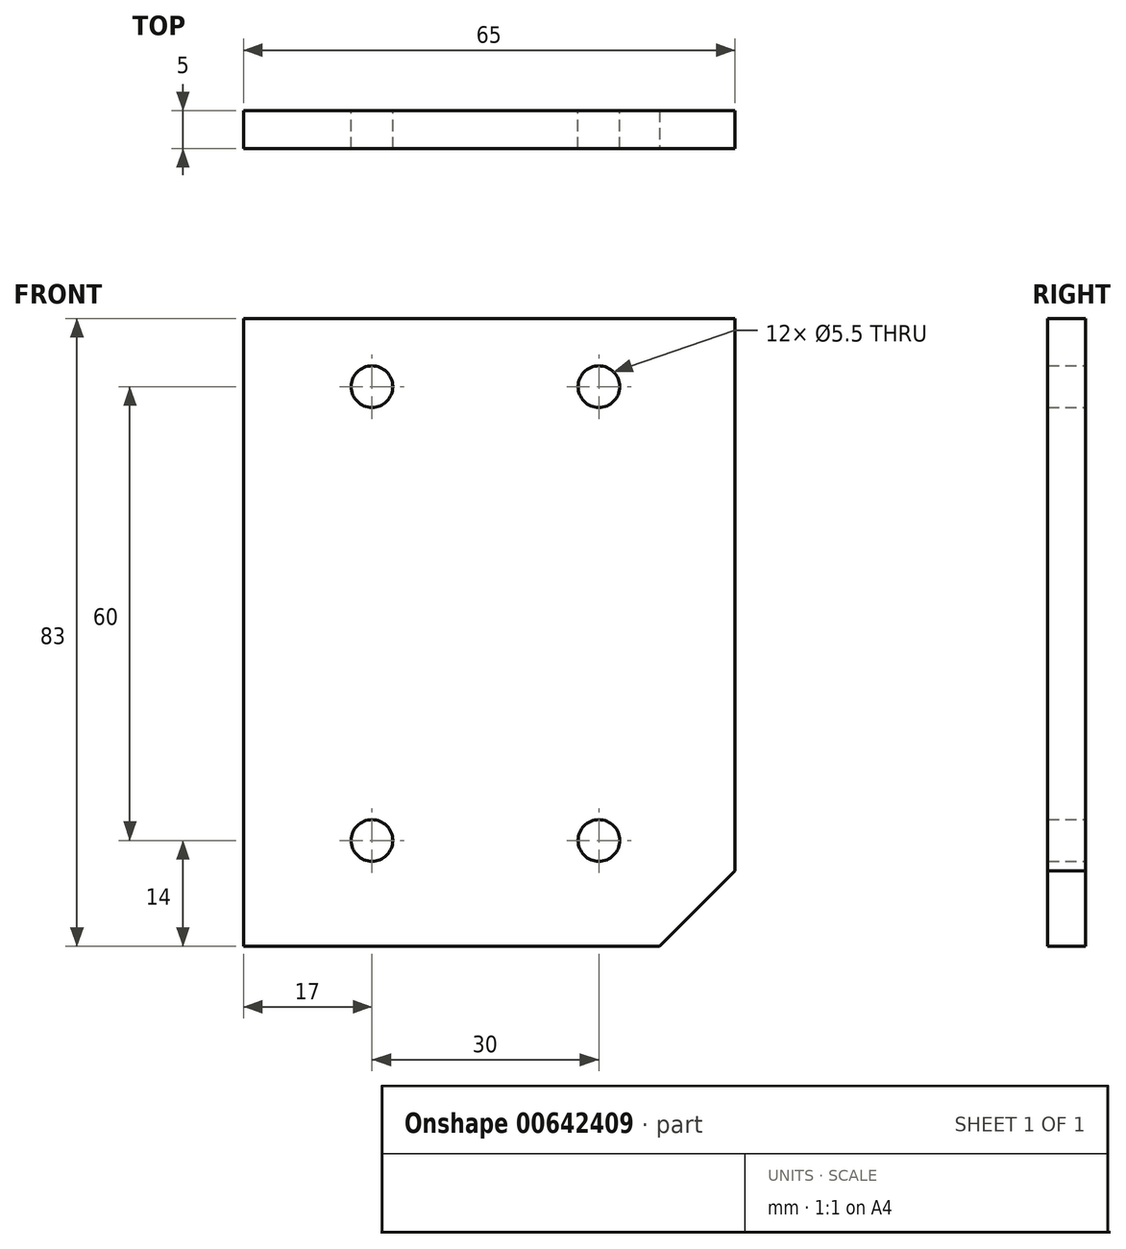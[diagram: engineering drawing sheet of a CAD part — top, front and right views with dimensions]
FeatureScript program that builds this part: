
annotation { "Feature Type Name" : "Feature", "Feature Type Description" : "" }
export const myFeature = defineFeature(function(context is Context, id is Id, definition is map)
    precondition{}
    {
        {
            var Q0;
            Q0=qCreatedBy(makeId("Front.planeOp"),FACE);
            var sketch = newSketch(context, id + "F0", { "sketchPlane" : qUnion([Q0])});
            skLineSegment(sketch, "E0.bottom", {"start": v(0, 0) * mm, "end": v(65, 0) * mm});
            skLineSegment(sketch, "E0.top", {"start": v(0, 83) * mm, "end": v(65, 83) * mm});
            skLineSegment(sketch, "E0.left", {"start": v(0, 0) * mm, "end": v(0, 83) * mm});
            skLineSegment(sketch, "E0.right", {"start": v(65, 0) * mm, "end": v(65, 83) * mm});
            skCircle(sketch, "E1", {"center": v(17, 74) * mm, "radius": 2.75 * mm});
            skCircle(sketch, "E2.0.1.0", {"center": v(17, 14) * mm, "radius": 2.75 * mm});
            skCircle(sketch, "E2.1.0.0", {"center": v(47, 74) * mm, "radius": 2.75 * mm});
            skCircle(sketch, "E2.1.1.0", {"center": v(47, 14) * mm, "radius": 2.75 * mm});
            skLineSegment(sketch, "E2.direction1", {"start": v(17, 74) * mm, "end": v(47, 74) * mm, "construction": true});
            skLineSegment(sketch, "E2.direction2", {"start": v(17, 74) * mm, "end": v(17, 14) * mm, "construction": true});
            skSolve(sketch);
        }
        {
            var Q0;
            Q0=makeQuery(id+"F0.imprint","IMPRINT",FACE,{"disambiguationData":[TD([[makeQuery(id+"F0.imprint","IMPRINT",EDGE,{"derivedFrom":sQuery(id+"F0.wireOp",EDGE,"E0.bottom")}),1.0]])]});
            extrude(context, id + "F1", {"entities" : qUnion([Q0]), "depth" : 5 * mm, "offsetDistance" : 25 * mm});
        }
        {
            var Q0;
            Q0=makeQuery(id+"F1.opExtrude","SWEPT_EDGE",EDGE,{"disambiguationData":[OSD([sQuery(id+"F0.wireOp",EDGE,"E0.bottom"),sQuery(id+"F0.wireOp",EDGE,"E0.right")])]});
            chamfer(context, id + "F2", {"entities" : qUnion([Q0]), "width" : 10 * mm, "tangentPropagation" : true});
        }
    });
